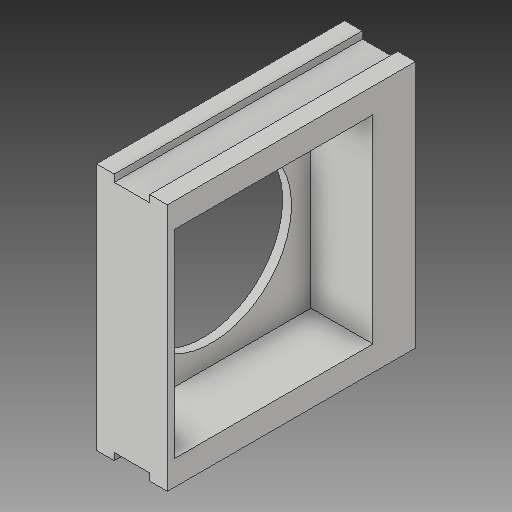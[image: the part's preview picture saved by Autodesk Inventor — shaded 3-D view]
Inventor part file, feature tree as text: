
AUTODESK INVENTOR PART (.ipt)
format: ipt  version: 2019 (Build 230136000, 136)  size: 139,776 bytes
history: native  units: in
note: dims shown in document units (in); Inventor stores cm internally (conversion verified against a paired STEP export)
features: sketch x8, other x3
ambient origin geometry x8: Origin, YZ Plane, XZ Plane, XY Plane, X Axis, Y Axis, Z Axis, Center Point
bodies: Solid1 (feature_tree)
feature tree (11):
  other  "LeadScrewBox.ipt"
  other  "Solid1::LeadScrewBox.ipt"
  other  "TaggingFeature1"
  sketch  "Sketch1"  dims[d0=0.3937in]
  sketch  "Sketch2"
  sketch  "Sketch3"
  sketch  "Sketch4"
  sketch  "Sketch5"
  sketch  "Sketch6"
  sketch  "Sketch7"
  sketch  "Sketch8"
